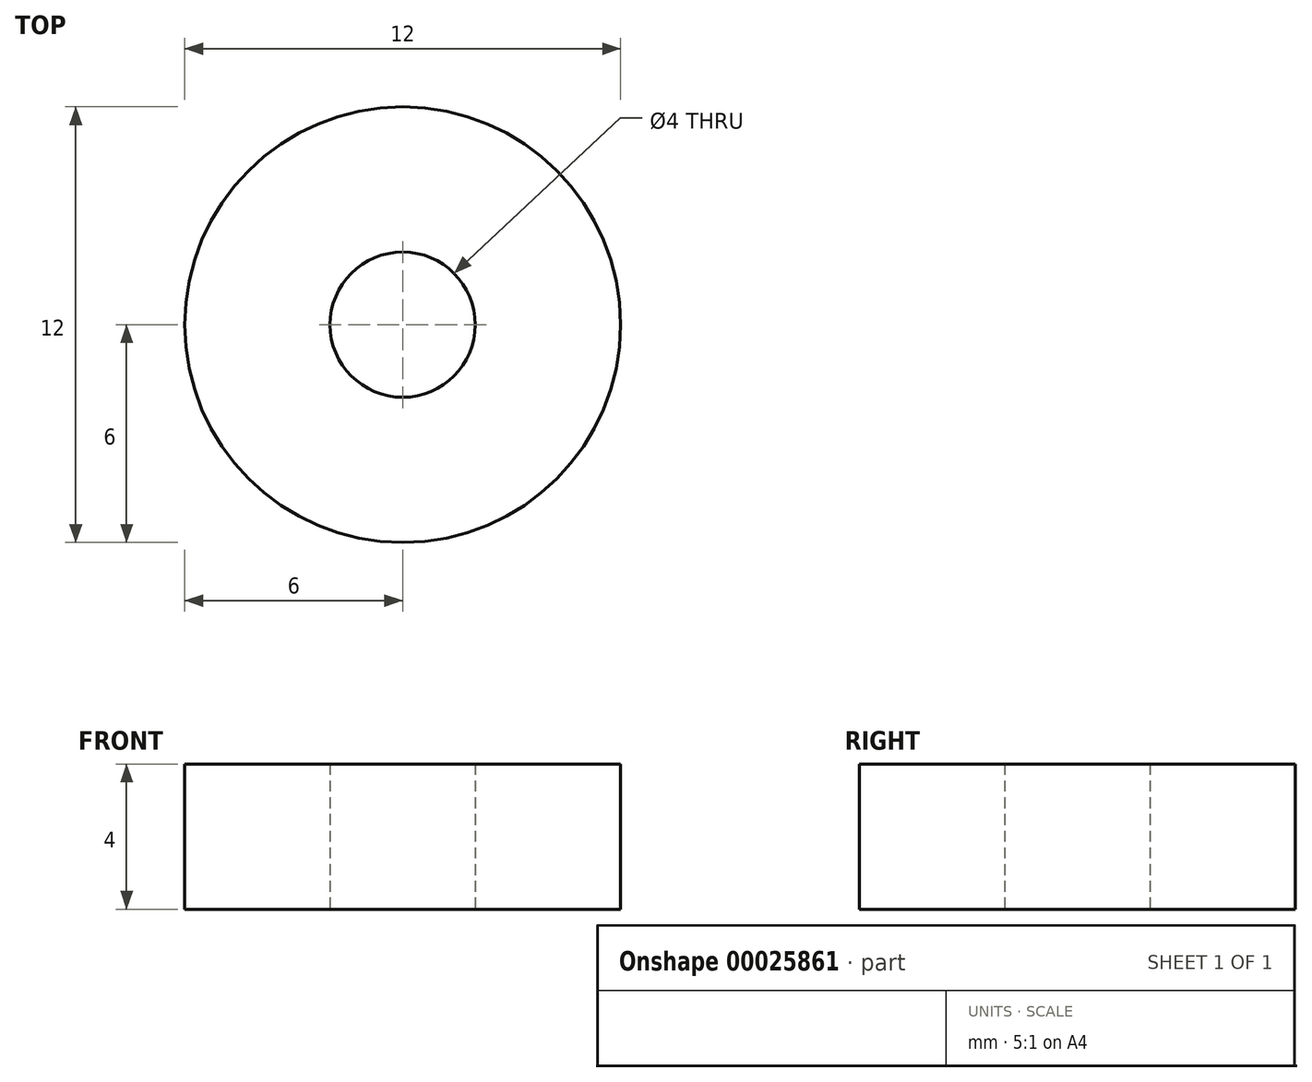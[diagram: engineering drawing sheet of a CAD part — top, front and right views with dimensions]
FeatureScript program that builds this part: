
annotation { "Feature Type Name" : "Feature", "Feature Type Description" : "" }
export const myFeature = defineFeature(function(context is Context, id is Id, definition is map)
    precondition{}
    {
        {
            var Q0;
            Q0=qCreatedBy(makeId("Top.planeOp"),FACE);
            var sketch = newSketch(context, id + "F0", { "sketchPlane" : qUnion([Q0])});
            skCircle(sketch, "E0", {"center": v(0, 0) * mm, "radius": 6 * mm});
            skCircle(sketch, "E1.0", {"center": v(0, 0) * mm, "radius": 2 * mm});
            skSolve(sketch);
        }
        {
            var Q0;
            Q0 = qSketchRegion(id + "F0", true);
            extrude(context, id + "F1", {"entities" : qUnion([Q0]), "depth" : 4 * mm});
        }
    });
